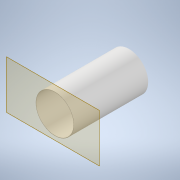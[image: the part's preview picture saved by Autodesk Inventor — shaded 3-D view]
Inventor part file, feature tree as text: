
AUTODESK INVENTOR PART (.ipt)
format: ipt  version: 2022 (Build 260153000, 153)  size: 110,080 bytes
history: native  units: mm
features: other x6, extrude x1, sketch x1, reference x1
ambient origin geometry x8: Origin, YZ Plane, XZ Plane, XY Plane, X Axis, Y Axis, Z Axis, Center Point
bodies: Body1 (feature_tree)
feature tree (9):
  other  "Твердое тело1"
  other  "РабПлоскость1"
  other  "РабПлоскость2"
  extrude  "Выдавливание1"  Depth=0.1mm
  sketch  "Эскиз1"
  reference  "Ссылка1"
  other  "<userpath>\Documents\Git\MZCAT_2024\MZCAT_4.iam"
  other  "MZCAT_4.iam"
  other  "base:1"
